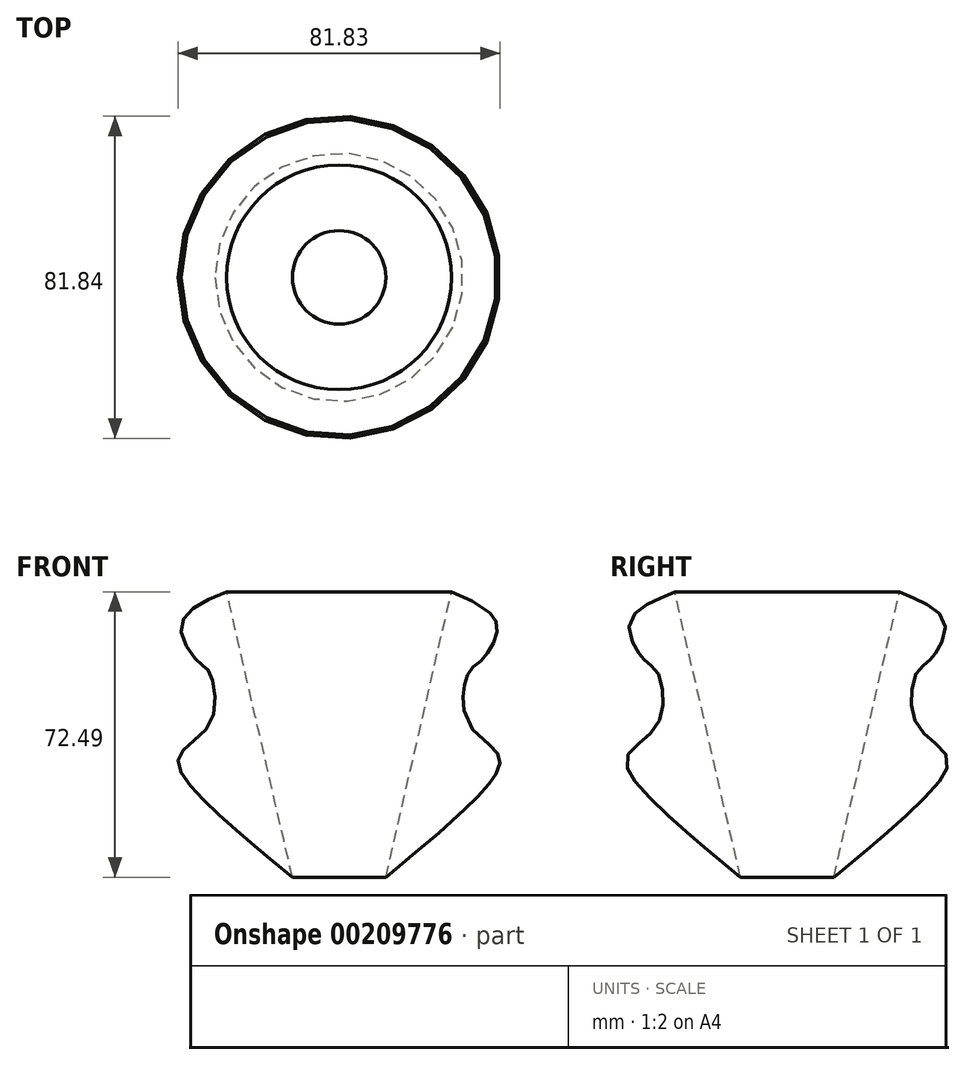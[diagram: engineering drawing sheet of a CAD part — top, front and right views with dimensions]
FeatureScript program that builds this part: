
annotation { "Feature Type Name" : "Feature", "Feature Type Description" : "" }
export const myFeature = defineFeature(function(context is Context, id is Id, definition is map)
    precondition{}
    {
        {
            var Q0;
            Q0=qCreatedBy(makeId("Front.planeOp"),FACE);
            var sketch = newSketch(context, id + "F0", { "sketchPlane" : qUnion([Q0])});
            skFitSpline(sketch, "E0", {"points": [v(-28.55, 33.2) * mm, v(-40.1, 24.86) * mm, v(-35.6, 15.24) * mm, v(-33.04, 13) * mm, v(-32.72, 0) * mm, v(-40.74, -8.82) * mm, v(-34.64, -19.4) * mm, v(-11.87, -39.3) * mm], "startDerivative": vector(-108.23, -44.35) * mm, "endDerivative": vector(112.55, -92.72) * mm});
            skLineSegment(sketch, "E1", {"start": v(-28.55, 33.2) * mm, "end": v(-11.87, -39.3) * mm});
            skLineSegment(sketch, "E2", {"start": v(0, 0) * mm, "end": v(0, 29.35) * mm, "construction": true});
            skSolve(sketch);
        }
        {
            var Q0;
            Q0=makeQuery(id+"F0.imprint","IMPRINT",FACE,{"disambiguationData":[TD([[makeQuery(id+"F0.imprint","IMPRINT",EDGE,{"derivedFrom":sQuery(id+"F0.wireOp",EDGE,"E0")}),1.0]])]});
            var Q1;
            Q1=sQuery(id+"F0.wireOp",EDGE,"E2");
            revolve(context, id + "F1", {"entities" : qUnion([Q0]), "axis" : qUnion([Q1]), "revolveType" : RevolveType.FULL});
        }
    });
